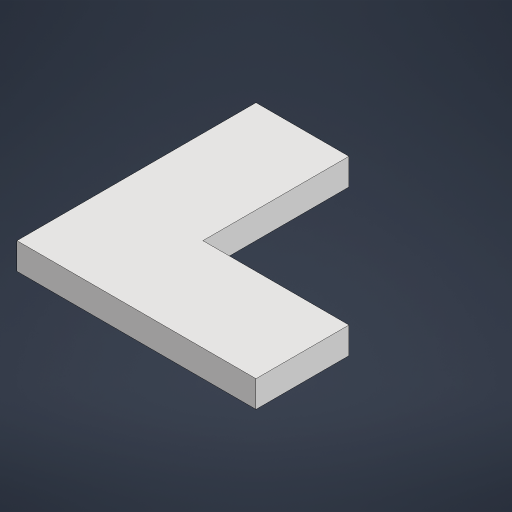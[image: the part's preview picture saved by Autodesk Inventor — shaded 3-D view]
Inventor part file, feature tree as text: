
AUTODESK INVENTOR PART (.ipt)
format: ipt  version: 2023.2 (Build 272271000, 271)  size: 159,232 bytes
history: native  units: in
note: dims shown in document units (in); Inventor stores cm internally (conversion verified against a paired STEP export)
features: extrude x1, sketch x1
ambient origin geometry x8: Origin, YZ Plane, XZ Plane, XY Plane, X Axis, Y Axis, Z Axis, Center Point
bodies: Solid1 (feature_tree)
feature tree (2):
  extrude  "Extrusion1"  Depth=7.0in
  sketch  "Sketch2"  dims[d3=18.0in d4=7.0in d5=2.0in d6=0.0in]
